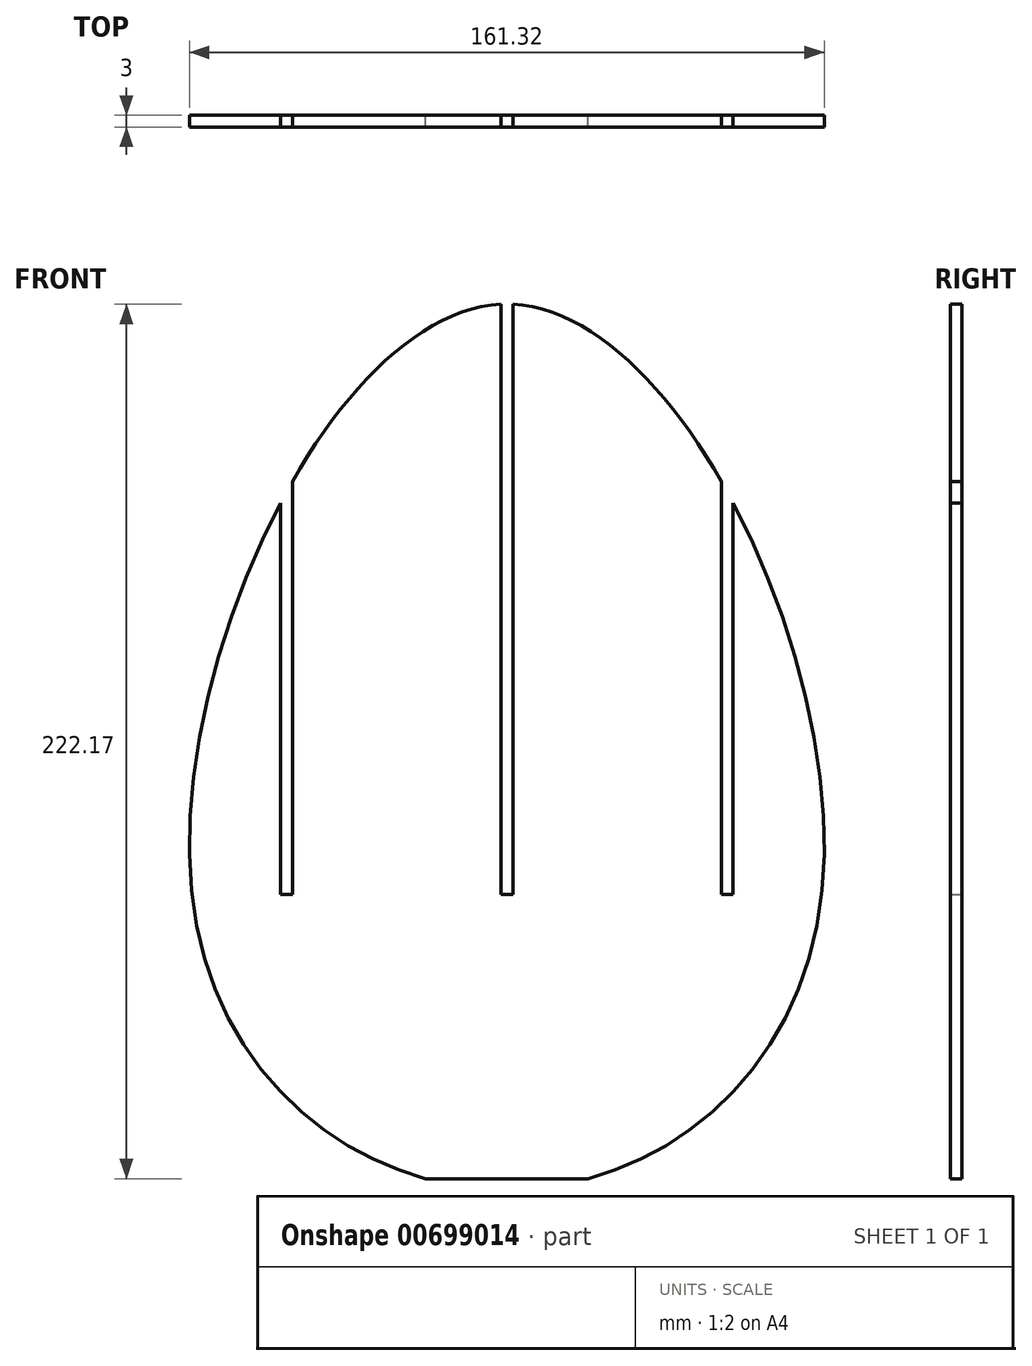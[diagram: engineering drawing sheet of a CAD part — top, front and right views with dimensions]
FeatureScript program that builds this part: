
annotation { "Feature Type Name" : "Feature", "Feature Type Description" : "" }
export const myFeature = defineFeature(function(context is Context, id is Id, definition is map)
    precondition{}
    {
        {
            var Q0;
            Q0=qCreatedBy(makeId("Front.planeOp"),FACE);
            var sketch = newSketch(context, id + "F0", { "sketchPlane" : qUnion([Q0])});
            skLineSegment(sketch, "E0", {"start": v(-169.34, 64.63) * mm, "end": v(-150.2, 64.63) * mm});
            skFitSpline(sketch, "E1", {"points": [v(107.32, 253.95) * mm, v(54.32, 153.95) * mm, v(107.32, 103.95) * mm, v(160.32, 153.95) * mm, v(107.32, 253.95) * mm]});
            skLineSegment(sketch, "E2.bottom", {"start": v(105.82, 153.95) * mm, "end": v(108.82, 153.95) * mm});
            skLineSegment(sketch, "E2.left", {"start": v(105.82, 153.95) * mm, "end": v(105.82, 103.97) * mm});
            skLineSegment(sketch, "E2.right", {"start": v(108.82, 153.95) * mm, "end": v(108.82, 103.97) * mm});
            skFitSpline(sketch, "E3", {"points": [v(-94.2, 9.83) * mm, v(-174.2, -140.17) * mm, v(-94.2, -215.17) * mm, v(-14.2, -140.17) * mm, v(-94.2, 9.83) * mm]});
            skLineSegment(sketch, "E4", {"start": v(-114.84, -212.37) * mm, "end": v(-73.56, -212.37) * mm});
            skFitSpline(sketch, "E5", {"points": [v(151.04, -25.2) * mm, v(98.04, -125.2) * mm, v(151.04, -175.2) * mm, v(204.04, -125.2) * mm, v(151.04, -25.2) * mm]});
            skLineSegment(sketch, "E6.bottom", {"start": v(149.54, -125.2) * mm, "end": v(152.54, -125.2) * mm});
            skLineSegment(sketch, "E7.bottom", {"start": v(-150.2, 136.84) * mm, "end": v(-147.2, 136.84) * mm});
            skLineSegment(sketch, "E7.left", {"start": v(-150.2, 136.84) * mm, "end": v(-150.2, 64.63) * mm});
            skLineSegment(sketch, "E7.right", {"start": v(-147.2, 136.84) * mm, "end": v(-147.2, 64.63) * mm});
            skLineSegment(sketch, "E8.bottom", {"start": v(-92.7, -140.17) * mm, "end": v(-95.7, -140.17) * mm});
            skLineSegment(sketch, "E8.left", {"start": v(-92.7, -140.17) * mm, "end": v(-92.7, 9.8) * mm});
            skLineSegment(sketch, "E8.right", {"start": v(-95.7, -140.17) * mm, "end": v(-95.7, 9.8) * mm});
            skLineSegment(sketch, "E9.bottom", {"start": v(152.54, -125.2) * mm, "end": v(149.54, -125.2) * mm});
            skLineSegment(sketch, "E9.left", {"start": v(152.54, -125.2) * mm, "end": v(152.54, -25.26) * mm});
            skLineSegment(sketch, "E9.right", {"start": v(149.54, -125.2) * mm, "end": v(149.54, -25.26) * mm});
            skLineSegment(sketch, "E10.bottom", {"start": v(-148.7, -140.17) * mm, "end": v(-151.7, -140.17) * mm});
            skLineSegment(sketch, "E10.left", {"start": v(-148.7, -140.17) * mm, "end": v(-148.7, -35.22) * mm});
            skLineSegment(sketch, "E10.right", {"start": v(-151.7, -140.17) * mm, "end": v(-151.7, -40.67) * mm});
            skLineSegment(sketch, "E11.bottom", {"start": v(-39.7, -140.17) * mm, "end": v(-36.7, -140.17) * mm});
            skLineSegment(sketch, "E11.left", {"start": v(-39.7, -140.17) * mm, "end": v(-39.7, -35.22) * mm});
            skLineSegment(sketch, "E11.right", {"start": v(-36.7, -140.17) * mm, "end": v(-36.7, -40.67) * mm});
            skLineSegment(sketch, "E12.bottom", {"start": v(-203.2, 136.84) * mm, "end": v(-206.2, 136.84) * mm});
            skLineSegment(sketch, "E12.left", {"start": v(-203.2, 136.84) * mm, "end": v(-203.2, 81.84) * mm});
            skLineSegment(sketch, "E12.right", {"start": v(-206.2, 136.84) * mm, "end": v(-206.2, 86.7) * mm});
            skLineSegment(sketch, "E13.bottom", {"start": v(-94.2, 136.84) * mm, "end": v(-91.2, 136.84) * mm});
            skLineSegment(sketch, "E13.left", {"start": v(-94.2, 136.84) * mm, "end": v(-94.2, 81.84) * mm});
            skLineSegment(sketch, "E13.right", {"start": v(-91.2, 136.84) * mm, "end": v(-91.2, 86.7) * mm});
            skFitSpline(sketch, "E14.trimOffspring", {"points": [v(-148.7, 286.84) * mm, v(-228.7, 136.84) * mm, v(-148.7, 61.84) * mm, v(-68.7, 136.84) * mm, v(-148.7, 286.84) * mm]});
            skLineSegment(sketch, "E15.trimOffspring", {"start": v(-147.2, 64.63) * mm, "end": v(-128.06, 64.63) * mm});
            skPoint(sketch, "E13.top.end.orphan", {"position": v(-91.2, 81.84) * mm});
            skPoint(sketch, "E16.orphan", {"position": v(-148.7, -30.17) * mm});
            skPoint(sketch, "E17.orphan", {"position": v(-92.7, 14.83) * mm});
            skPoint(sketch, "E18.orphan", {"position": v(-36.7, -30.17) * mm});
            skPoint(sketch, "E19.orphan", {"position": v(149.54, -22.3) * mm});
            skSolve(sketch);
        }
        {
            var Q0;
            {var subQ0=sQuery(id+"F0.wireOp",EDGE,"8ec7edd3-c6ee-493f-bf12-1f4fd8b1b25e");Q0=makeQuery(id+"F0.imprint","IMPRINT",FACE,{"disambiguationData":[TD([[makeQuery(id+"F0.imprint","IMPRINT",EDGE,{"derivedFrom":subQ0}),1.0]])]});}
            var Q1;
            {var subQ0=sQuery(id+"F0.wireOp",EDGE,"8ec7edd3-c6ee-493f-bf12-1f4fd8b1b25e");Q1=makeQuery(id+"F0.imprint","IMPRINT",FACE,{"disambiguationData":[TD([[makeQuery(id+"F0.imprint","IMPRINT",EDGE,{"derivedFrom":subQ0}),-1.0]])]});}
            var Q2;
            {var subQ1=sQuery(id+"F0.wireOp",EDGE,"E8.top");Q2=makeQuery(id+"F0.imprint","IMPRINT",FACE,{"disambiguationData":[TD([[makeQuery(id+"F0.imprint","IMPRINT",EDGE,{"derivedFrom":subQ1}),1.0]])]});}
            var Q3;
            {var subQ0=sQuery(id+"F0.wireOp",EDGE,"db233980-1812-4aea-802b-383a19f5e98a");Q3=makeQuery(id+"F0.imprint","IMPRINT",FACE,{"disambiguationData":[TD([[makeQuery(id+"F0.imprint","IMPRINT",EDGE,{"derivedFrom":subQ0}),-1.0]])]});}
            var Q4;
            {var subQ0=sQuery(id+"F0.wireOp",EDGE,"db233980-1812-4aea-802b-383a19f5e98a");Q4=makeQuery(id+"F0.imprint","IMPRINT",FACE,{"disambiguationData":[TD([[makeQuery(id+"F0.imprint","IMPRINT",EDGE,{"derivedFrom":subQ0}),1.0]])]});}
            var Q5;
            {var subQ7=sQuery(id+"F0.wireOp",EDGE,"eca1b38f-5b18-418b-8c6b-b31e0e3a653b");Q5=makeQuery(id+"F0.imprint","IMPRINT",FACE,{"disambiguationData":[TD([[makeQuery(id+"F0.imprint","IMPRINT",EDGE,{"derivedFrom":subQ7}),1.0]])]});}
            var Q6;
            {var subQ7=sQuery(id+"F0.wireOp",EDGE,"eca1b38f-5b18-418b-8c6b-b31e0e3a653b");Q6=makeQuery(id+"F0.imprint","IMPRINT",FACE,{"disambiguationData":[TD([[makeQuery(id+"F0.imprint","IMPRINT",EDGE,{"derivedFrom":subQ7}),-1.0]])]});}
            var Q7;
            {var subQ10=sQuery(id+"F0.wireOp",EDGE,"E10.bottom");Q7=makeQuery(id+"F0.imprint","IMPRINT",FACE,{"disambiguationData":[TD([[makeQuery(id+"F0.imprint","IMPRINT",EDGE,{"derivedFrom":subQ10}),1.0]])]});}
            var Q8;
            {var subQ14=sQuery(id+"F0.wireOp",EDGE,"E11.bottom");Q8=makeQuery(id+"F0.imprint","IMPRINT",FACE,{"disambiguationData":[TD([[makeQuery(id+"F0.imprint","IMPRINT",EDGE,{"derivedFrom":subQ14}),-1.0]])]});}
            extrude(context, id + "F1", {"entities" : qUnion([Q0, Q1, Q2, Q3, Q4, Q5, Q6, Q7, Q8]), "depth" : 3 * mm, "offsetDistance" : 25 * mm});
        }
    });
